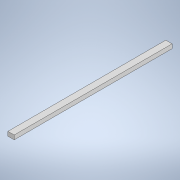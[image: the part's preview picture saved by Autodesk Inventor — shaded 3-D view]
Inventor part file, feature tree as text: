
AUTODESK INVENTOR PART (.ipt)
format: ipt  version: 2020 (Build 240168000, 168)  size: 98,304 bytes
history: native  units: mm
features: other x1, extrude x1, sketch x1
ambient origin geometry x8: Origin, YZ Plane, XZ Plane, XY Plane, X Axis, Y Axis, Z Axis, Center Point
bodies: Solid1 (feature_tree)
feature tree (3):
  other  "<userpath>\Documents\Development\paragon-printer\Paragon Printer Parameters.xlsx"
  extrude  "Extrusion1"  Depth=8.0mm
  sketch  "Sketch3"  dims[d0=12.0mm d1=8.0mm d2=300.0mm d3=0.0mm]
